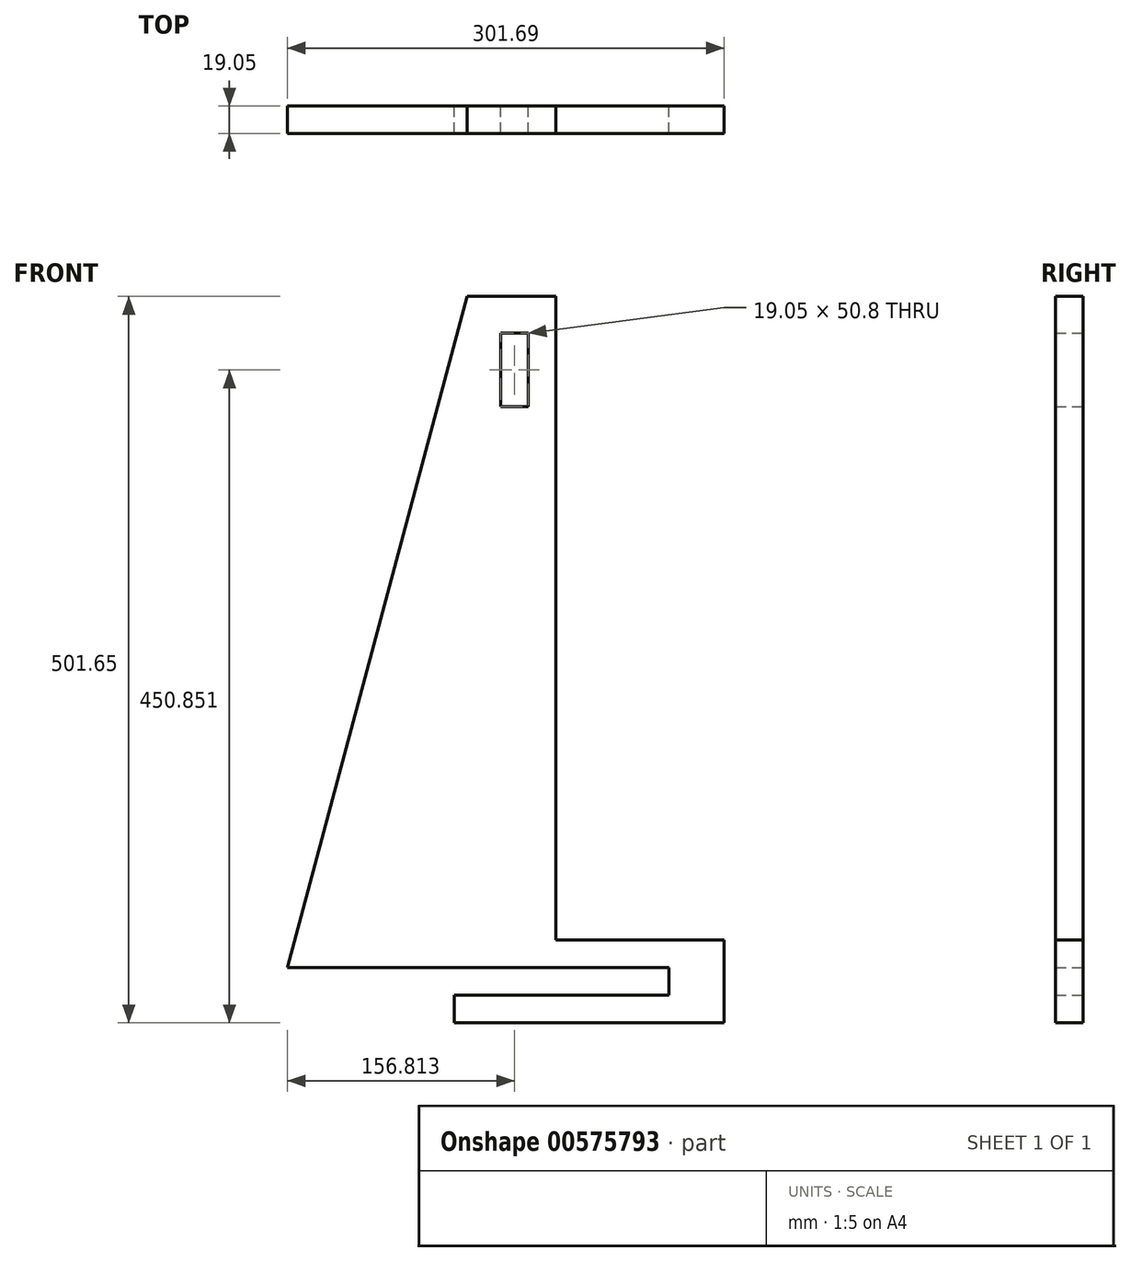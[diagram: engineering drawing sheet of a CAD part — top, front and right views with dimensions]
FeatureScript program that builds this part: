
annotation { "Feature Type Name" : "Feature", "Feature Type Description" : "" }
export const myFeature = defineFeature(function(context is Context, id is Id, definition is map)
    precondition{}
    {
        {
            var Q0;
            Q0=qCreatedBy(makeId("Front.planeOp"),FACE);
            var sketch = newSketch(context, id + "F0", { "sketchPlane" : qUnion([Q0])});
            skLineSegment(sketch, "E0", {"start": v(-238.45, 27.42) * mm, "end": v(-299.63, 27.42) * mm});
            skLineSegment(sketch, "E1", {"start": v(-276.55, 2.02) * mm, "end": v(-257.5, 2.02) * mm});
            skLineSegment(sketch, "E2", {"start": v(-257.5, 2.02) * mm, "end": v(-257.5, -48.78) * mm});
            skLineSegment(sketch, "E3", {"start": v(-257.5, -48.78) * mm, "end": v(-276.55, -48.78) * mm});
            skLineSegment(sketch, "E4", {"start": v(-276.55, -48.78) * mm, "end": v(-276.55, 2.02) * mm});
            skLineSegment(sketch, "E5", {"start": v(-423.84, -436.13) * mm, "end": v(-299.63, 27.42) * mm});
            skLineSegment(sketch, "E6", {"start": v(-423.84, -436.13) * mm, "end": v(-160.25, -436.13) * mm});
            skLineSegment(sketch, "E7", {"start": v(-238.45, 27.42) * mm, "end": v(-238.45, -417.08) * mm});
            skLineSegment(sketch, "E8", {"start": v(-238.45, -417.08) * mm, "end": v(-122.15, -417.08) * mm});
            skLineSegment(sketch, "E9", {"start": v(-122.15, -417.08) * mm, "end": v(-122.15, -474.23) * mm});
            skLineSegment(sketch, "E10", {"start": v(-122.15, -474.23) * mm, "end": v(-308.63, -474.23) * mm});
            skLineSegment(sketch, "E11", {"start": v(-308.63, -474.23) * mm, "end": v(-308.63, -455.18) * mm});
            skLineSegment(sketch, "E12", {"start": v(-308.63, -455.18) * mm, "end": v(-160.25, -455.18) * mm});
            skLineSegment(sketch, "E13", {"start": v(-160.25, -455.18) * mm, "end": v(-160.25, -436.13) * mm});
            skSolve(sketch);
        }
        {
            var Q0;
            Q0=makeQuery(id+"F0.imprint","IMPRINT",FACE,{"disambiguationData":[TD([[makeQuery(id+"F0.imprint","IMPRINT",EDGE,{"derivedFrom":sQuery(id+"F0.wireOp",EDGE,"E0")}),1.0]])]});
            extrude(context, id + "F1", {"entities" : qUnion([Q0]), "depth" : 19.05 * mm, "offsetDistance" : 25.4 * mm});
        }
    });
